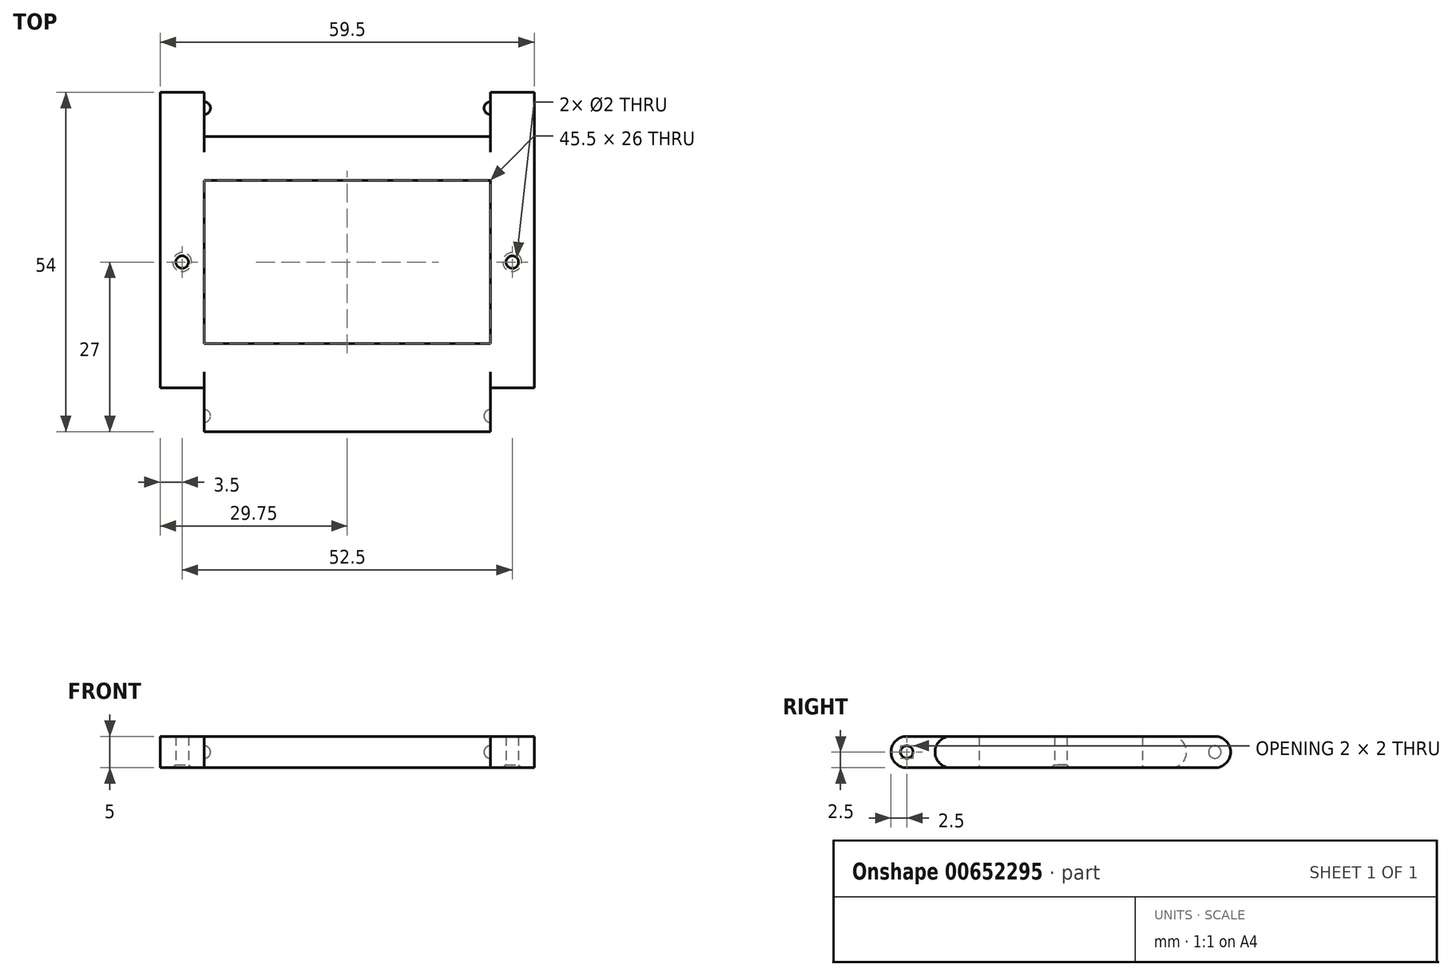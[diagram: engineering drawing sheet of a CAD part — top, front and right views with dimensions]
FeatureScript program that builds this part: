
annotation { "Feature Type Name" : "Feature", "Feature Type Description" : "" }
export const myFeature = defineFeature(function(context is Context, id is Id, definition is map)
    precondition{}
    {
        {
            var Q0;
            Q0=qCreatedBy(makeId("Top.planeOp"),FACE);
            var sketch = newSketch(context, id + "F0", { "sketchPlane" : qUnion([Q0])});
            skLineSegment(sketch, "E0.bottom", {"start": v(29.75, -20) * mm, "end": v(-29.75, -20) * mm});
            skLineSegment(sketch, "E0.top", {"start": v(29.75, 20) * mm, "end": v(-29.75, 20) * mm});
            skLineSegment(sketch, "E0.left", {"start": v(29.75, -20) * mm, "end": v(29.75, 20) * mm});
            skLineSegment(sketch, "E0.right", {"start": v(-29.75, -20) * mm, "end": v(-29.75, 20) * mm});
            skPoint(sketch, "E0.middle", {"position": v(0, 0) * mm});
            skLineSegment(sketch, "E1.bottom", {"start": v(22.75, -13) * mm, "end": v(-22.75, -13) * mm});
            skLineSegment(sketch, "E1.top", {"start": v(22.75, 13) * mm, "end": v(-22.75, 13) * mm});
            skLineSegment(sketch, "E1.left", {"start": v(22.75, -13) * mm, "end": v(22.75, 13) * mm});
            skLineSegment(sketch, "E1.right", {"start": v(-22.75, -13) * mm, "end": v(-22.75, 13) * mm});
            skLineSegment(sketch, "E2", {"start": v(-29.75, 20) * mm, "end": v(-29.75, 27) * mm});
            skLineSegment(sketch, "E3", {"start": v(-29.75, 27) * mm, "end": v(-22.75, 27) * mm});
            skLineSegment(sketch, "E4", {"start": v(-22.75, 27) * mm, "end": v(-22.75, 20) * mm});
            skLineSegment(sketch, "E5", {"start": v(-22.75, 20) * mm, "end": v(-22.75, 20) * mm});
            skLineSegment(sketch, "E6", {"start": v(29.75, 20) * mm, "end": v(29.75, 27) * mm});
            skLineSegment(sketch, "E7", {"start": v(29.75, 27) * mm, "end": v(22.75, 27) * mm});
            skLineSegment(sketch, "E8", {"start": v(22.75, 27) * mm, "end": v(22.75, 20) * mm});
            skLineSegment(sketch, "E9", {"start": v(-29.75, -20) * mm, "end": v(-29.75, -20) * mm});
            skLineSegment(sketch, "E10", {"start": v(-22.75, -20) * mm, "end": v(-22.75, -27) * mm});
            skLineSegment(sketch, "E11", {"start": v(22.75, -27) * mm, "end": v(-22.75, -27) * mm});
            skLineSegment(sketch, "E12", {"start": v(22.75, -27) * mm, "end": v(22.75, -20) * mm});
            skPoint(sketch, "E13", {"position": v(-26.25, 0) * mm});
            skPoint(sketch, "E14", {"position": v(26.25, 0) * mm});
            skSolve(sketch);
        }
        {
            var Q0;
            {var subQ0=sQuery(id+"F0.wireOp",EDGE,"E10");Q0=makeQuery(id+"F0.imprint","IMPRINT",FACE,{"disambiguationData":[TD([[makeQuery(id+"F0.imprint","IMPRINT",EDGE,{"derivedFrom":subQ0}),1.0]])]});}
            var Q1;
            {var subQ1=sQuery(id+"F0.wireOp",EDGE,"E0.left");Q1=makeQuery(id+"F0.imprint","IMPRINT",FACE,{"disambiguationData":[TD([[makeQuery(id+"F0.imprint","IMPRINT",EDGE,{"derivedFrom":subQ1}),1.0]])]});}
            var Q2;
            {var subQ0=sQuery(id+"F0.wireOp",EDGE,"E6");Q2=makeQuery(id+"F0.imprint","IMPRINT",FACE,{"disambiguationData":[TD([[makeQuery(id+"F0.imprint","IMPRINT",EDGE,{"derivedFrom":subQ0}),1.0]])]});}
            var Q3;
            {var subQ0=sQuery(id+"F0.wireOp",EDGE,"E2");Q3=makeQuery(id+"F0.imprint","IMPRINT",FACE,{"disambiguationData":[TD([[makeQuery(id+"F0.imprint","IMPRINT",EDGE,{"derivedFrom":subQ0}),-1.0]])]});}
            extrude(context, id + "F1", {"entities" : qUnion([Q0, Q1, Q2, Q3]), "depth" : 5 * mm, "offsetDistance" : 25 * mm});
        }
        {
            var Q0;
            Q0=makeQuery(id+"F1.opExtrude","CAP_EDGE",EDGE,{"disambiguationData":[OSD([sQuery(id+"F0.wireOp",EDGE,"E0.top")])],"isStart":false});
            var Q1;
            Q1=makeQuery(id+"F1.opExtrude","CAP_EDGE",EDGE,{"disambiguationData":[OSD([sQuery(id+"F0.wireOp",EDGE,"E0.top")])],"isStart":true});
            var Q2;
            Q2=makeQuery(id+"F1.opExtrude","CAP_EDGE",EDGE,{"disambiguationData":[OSD([sQuery(id+"F0.wireOp",EDGE,"E3")])],"isStart":false});
            var Q3;
            Q3=makeQuery(id+"F1.opExtrude","CAP_EDGE",EDGE,{"disambiguationData":[OSD([sQuery(id+"F0.wireOp",EDGE,"E3")])],"isStart":true});
            var Q4;
            Q4=makeQuery(id+"F1.opExtrude","CAP_EDGE",EDGE,{"disambiguationData":[OSD([sQuery(id+"F0.wireOp",EDGE,"E7")])],"isStart":false});
            var Q5;
            Q5=makeQuery(id+"F1.opExtrude","CAP_EDGE",EDGE,{"disambiguationData":[OSD([sQuery(id+"F0.wireOp",EDGE,"E7")])],"isStart":true});
            var Q6;
            Q6=makeQuery(id+"F1.opExtrude","CAP_EDGE",EDGE,{"disambiguationData":[OSD([sQuery(id+"F0.wireOp",EDGE,"E11")])],"isStart":false});
            var Q7;
            {var subQ0=sQuery(id+"F0.wireOp",EDGE,"E0.bottom");Q7=makeQuery(id+"F1.opExtrude","CAP_EDGE",EDGE,{"disambiguationData":[OSD([subQ0]),TDD([makeQuery(id+"F0.imprint","IMPRINT",EDGE,{"disambiguationData":[TD([[makeQuery(id+"F0.imprint","INTERSECT",VERTEX,{"derivedFrom":[subQ0,sQuery(id+"F0.wireOp",EDGE,"E0.right")]}),1.0]])],"derivedFrom":subQ0})])],"isStart":false});}
            var Q8;
            {var subQ0=sQuery(id+"F0.wireOp",EDGE,"E0.bottom");Q8=makeQuery(id+"F1.opExtrude","CAP_EDGE",EDGE,{"disambiguationData":[OSD([subQ0]),TDD([makeQuery(id+"F0.imprint","IMPRINT",EDGE,{"disambiguationData":[TD([[makeQuery(id+"F0.imprint","INTERSECT",VERTEX,{"derivedFrom":[subQ0,sQuery(id+"F0.wireOp",EDGE,"E0.left")]}),-1.0]])],"derivedFrom":subQ0})])],"isStart":false});}
            var Q9;
            Q9=makeQuery(id+"F1.opExtrude","CAP_EDGE",EDGE,{"disambiguationData":[OSD([sQuery(id+"F0.wireOp",EDGE,"E11")])],"isStart":true});
            var Q10;
            {var subQ0=sQuery(id+"F0.wireOp",EDGE,"E0.bottom");Q10=makeQuery(id+"F1.opExtrude","CAP_EDGE",EDGE,{"disambiguationData":[OSD([subQ0]),TDD([makeQuery(id+"F0.imprint","IMPRINT",EDGE,{"disambiguationData":[TD([[makeQuery(id+"F0.imprint","INTERSECT",VERTEX,{"derivedFrom":[subQ0,sQuery(id+"F0.wireOp",EDGE,"E0.left")]}),-1.0]])],"derivedFrom":subQ0})])],"isStart":true});}
            var Q11;
            {var subQ0=sQuery(id+"F0.wireOp",EDGE,"E0.bottom");Q11=makeQuery(id+"F1.opExtrude","CAP_EDGE",EDGE,{"disambiguationData":[OSD([subQ0]),TDD([makeQuery(id+"F0.imprint","IMPRINT",EDGE,{"disambiguationData":[TD([[makeQuery(id+"F0.imprint","INTERSECT",VERTEX,{"derivedFrom":[subQ0,sQuery(id+"F0.wireOp",EDGE,"E0.right")]}),1.0]])],"derivedFrom":subQ0})])],"isStart":true});}
            fillet(context, id + "F2", {"entities" : qUnion([Q0, Q1, Q2, Q3, Q4, Q5, Q6, Q7, Q8, Q9, Q10, Q11]), "radius" : 2.5 * mm, "tangentPropagation" : true, "allowEdgeOverflow" : false});
        }
        {
            var Q0;
            Q0=makeQuery(id+"F1.opExtrude","SWEPT_FACE",FACE,{"disambiguationData":[OSD([sQuery(id+"F0.wireOp",EDGE,"E4")])]});
            var sketch = newSketch(context, id + "F3", { "sketchPlane" : qUnion([Q0])});
            skCircle(sketch, "E15", {"center": v(24.5, 2.5) * mm, "radius": 1 * mm});
            skSolve(sketch);
        }
        {
            var Q0;
            Q0=makeQuery(id+"F1.opExtrude","SWEPT_FACE",FACE,{"disambiguationData":[OSD([sQuery(id+"F0.wireOp",EDGE,"E8")])]});
            var sketch = newSketch(context, id + "F4", { "sketchPlane" : qUnion([Q0])});
            skCircle(sketch, "E16", {"center": v(-24.5, 2.5) * mm, "radius": 1 * mm});
            skSolve(sketch);
        }
        {
            var Q0;
            Q0=makeQuery(id+"F3.imprint","IMPRINT",FACE,{"disambiguationData":[TD([[makeQuery(id+"F3.imprint","IMPRINT",EDGE,{"derivedFrom":sQuery(id+"F3.wireOp",EDGE,"E15")}),1.0]])]});
            var Q1;
            Q1=makeQuery(id+"F4.imprint","IMPRINT",FACE,{"disambiguationData":[TD([[makeQuery(id+"F4.imprint","IMPRINT",EDGE,{"derivedFrom":sQuery(id+"F4.wireOp",EDGE,"E16")}),1.0]])]});
            extrude(context, id + "F5", {"entities" : qUnion([Q0, Q1]), "operationType" : NewBodyOperationType.ADD, "oppositeDirection" : true, "depth" : 1 * mm, "offsetDistance" : 25 * mm, "hasSecondDirection" : true, "secondDirectionOppositeDirection" : false, "secondDirectionDepth" : 1 * mm});
        }
        {
            var Q0;
            Q0=makeQuery(id+"F5.opExtrude","CAP_EDGE",EDGE,{"disambiguationData":[OSD([sQuery(id+"F3.wireOp",EDGE,"E15")])],"isStart":true});
            var Q1;
            Q1=makeQuery(id+"F5.opExtrude","CAP_EDGE",EDGE,{"disambiguationData":[OSD([sQuery(id+"F4.wireOp",EDGE,"E16")])],"isStart":false});
            fillet(context, id + "F6", {"entities" : qUnion([Q0, Q1]), "radius" : 1 * mm, "tangentPropagation" : true, "allowEdgeOverflow" : false});
        }
        {
            var Q0;
            Q0=makeQuery(id+"F1.opExtrude","SWEPT_FACE",FACE,{"disambiguationData":[OSD([sQuery(id+"F0.wireOp",EDGE,"E12")])]});
            var sketch = newSketch(context, id + "F7", { "sketchPlane" : qUnion([Q0])});
            skCircle(sketch, "E17", {"center": v(-24.5, 2.5) * mm, "radius": 1 * mm});
            skSolve(sketch);
        }
        {
            var Q0;
            Q0=makeQuery(id+"F1.opExtrude","SWEPT_FACE",FACE,{"disambiguationData":[OSD([sQuery(id+"F0.wireOp",EDGE,"E10")])]});
            var sketch = newSketch(context, id + "F8", { "sketchPlane" : qUnion([Q0])});
            skCircle(sketch, "E18", {"center": v(24.5, 2.5) * mm, "radius": 1 * mm});
            skSolve(sketch);
        }
        {
            var Q0;
            Q0=makeQuery(id+"F8.imprint","IMPRINT",FACE,{"disambiguationData":[TD([[makeQuery(id+"F8.imprint","IMPRINT",EDGE,{"derivedFrom":sQuery(id+"F8.wireOp",EDGE,"E18")}),1.0]])]});
            var Q1;
            Q1=makeQuery(id+"F7.imprint","IMPRINT",FACE,{"disambiguationData":[TD([[makeQuery(id+"F7.imprint","IMPRINT",EDGE,{"derivedFrom":sQuery(id+"F7.wireOp",EDGE,"E17")}),1.0]])]});
            extrude(context, id + "F9", {"entities" : qUnion([Q0, Q1]), "operationType" : NewBodyOperationType.REMOVE, "oppositeDirection" : true, "depth" : 1 * mm, "offsetDistance" : 25 * mm, "hasSecondDirection" : true, "secondDirectionOppositeDirection" : false, "secondDirectionDepth" : 1 * mm});
        }
        {
            var Q0;
            Q0=makeQuery(id+"F9.boolean.opBoolean","COPY",EDGE,{"derivedFrom":makeQuery(id+"F9.opExtrude","CAP_EDGE",EDGE,{"disambiguationData":[OSD([sQuery(id+"F8.wireOp",EDGE,"E18")])],"isStart":false})});
            var Q1;
            Q1=makeQuery(id+"F9.boolean.opBoolean","COPY",EDGE,{"derivedFrom":makeQuery(id+"F9.opExtrude","CAP_EDGE",EDGE,{"disambiguationData":[OSD([sQuery(id+"F7.wireOp",EDGE,"E17")])],"isStart":true})});
            fillet(context, id + "F10", {"entities" : qUnion([Q0, Q1]), "radius" : 1 * mm, "tangentPropagation" : true, "allowEdgeOverflow" : false});
        }
        {
            var Q0;
            Q0=sQuery(id+"F0.wireOp",VERTEX,"E14");
            var Q1;
            Q1=sQuery(id+"F0.wireOp",VERTEX,"E13");
            var Q2;
            Q2=sQuery(id+"F0.wireOp",VERTEX,"8111c63c-2aff-4b5e-8321-e08c87799ba0");
            var Q3;
            Q3=sQuery(id+"F0.wireOp",VERTEX,"8a581a4e-eadc-4c07-8136-a46bb6d99a40");
            var Q4;
            Q4=makeQuery(id+"F1.opExtrude","SWEPT_BODY",BODY,{"disambiguationData":[OSD([sQuery(id+"F0.wireOp",EDGE,"E0.bottom"),sQuery(id+"F0.wireOp",EDGE,"E0.top"),sQuery(id+"F0.wireOp",EDGE,"E0.left"),sQuery(id+"F0.wireOp",EDGE,"E0.right"),sQuery(id+"F0.wireOp",EDGE,"E1.bottom"),sQuery(id+"F0.wireOp",EDGE,"E1.top"),sQuery(id+"F0.wireOp",EDGE,"E1.left"),sQuery(id+"F0.wireOp",EDGE,"E1.right"),sQuery(id+"F0.wireOp",EDGE,"E2"),sQuery(id+"F0.wireOp",EDGE,"E3"),sQuery(id+"F0.wireOp",EDGE,"E4"),sQuery(id+"F0.wireOp",EDGE,"E6"),sQuery(id+"F0.wireOp",EDGE,"E7"),sQuery(id+"F0.wireOp",EDGE,"E8"),sQuery(id+"F0.wireOp",EDGE,"E10"),sQuery(id+"F0.wireOp",EDGE,"E11"),sQuery(id+"F0.wireOp",EDGE,"E12")])]});
            hole(context, id + "F11", {"style" : HoleStyle.C_SINK, "endStyle" : HoleEndStyle.THROUGH, "oppositeDirection" : true, "holeDiameter" : 2 * mm, "cSinkDiameter" : 3 * mm, "cSinkAngle" : 90 * degree, "majorDiameter" : 5 * mm, "isTappedThrough" : true, "tappedDepth" : 12 * mm, "tapClearance" : 3, "locations" : qUnion([Q0, Q1, Q2, Q3]), "scope" : qUnion([Q4])});
        }
    });
